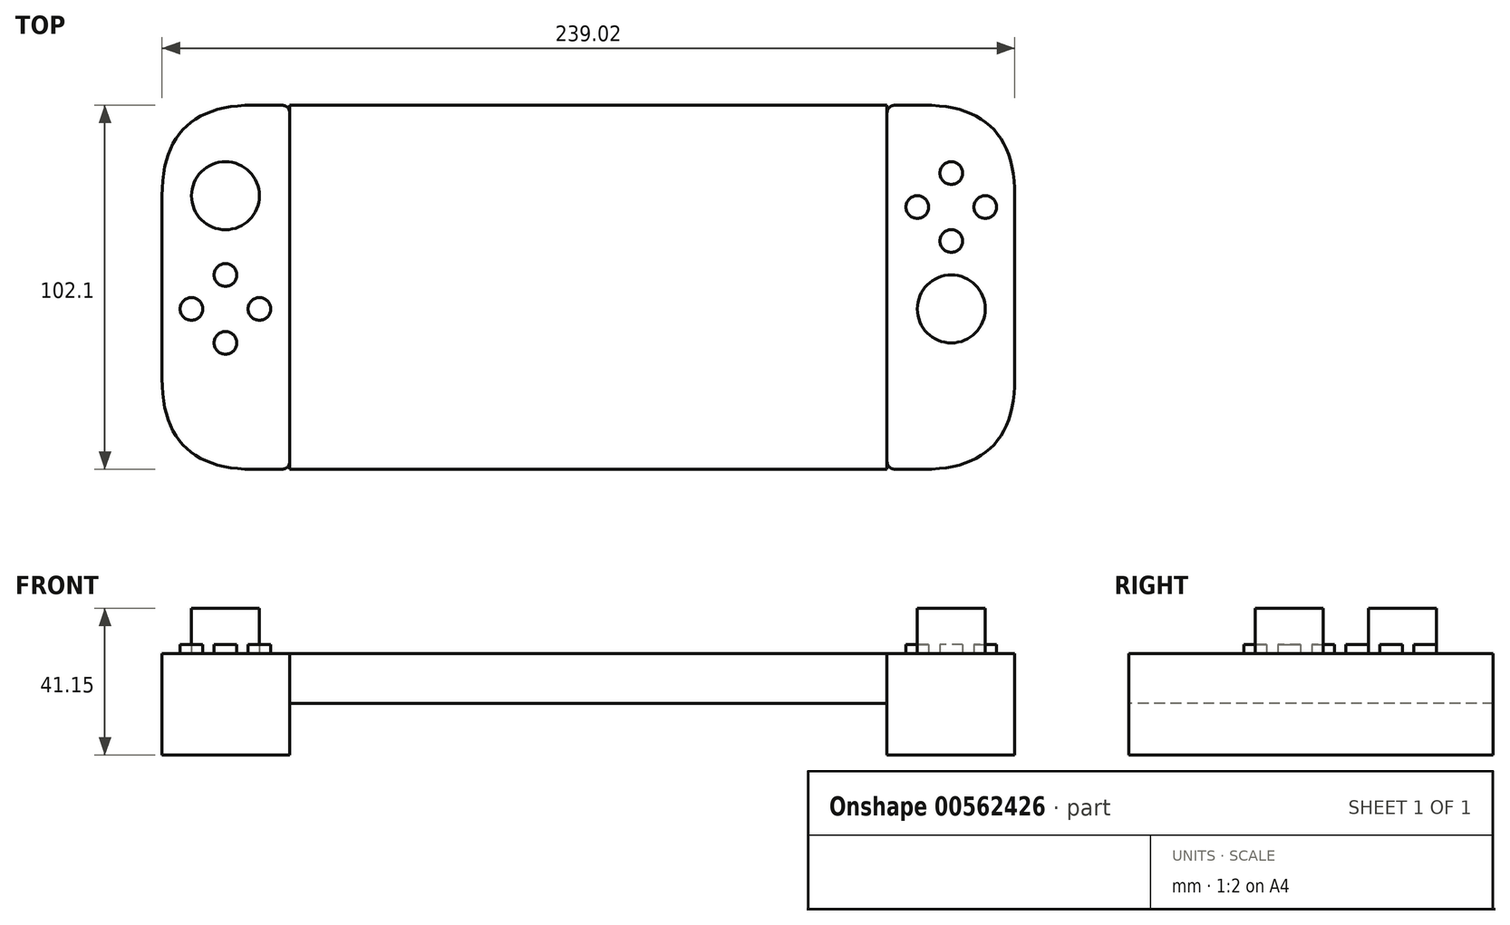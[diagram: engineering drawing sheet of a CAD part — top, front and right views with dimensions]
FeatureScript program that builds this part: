
annotation { "Feature Type Name" : "Feature", "Feature Type Description" : "" }
export const myFeature = defineFeature(function(context is Context, id is Id, definition is map)
    precondition{}
    {
        {
            var Q0;
            Q0=qCreatedBy(makeId("Top.planeOp"),FACE);
            var sketch = newSketch(context, id + "F0", { "sketchPlane" : qUnion([Q0])});
            skLineSegment(sketch, "E0.bottom", {"start": v(83.7, 51.05) * mm, "end": v(-83.7, 51.05) * mm});
            skLineSegment(sketch, "E0.top", {"start": v(83.7, -51.05) * mm, "end": v(-83.7, -51.05) * mm});
            skLineSegment(sketch, "E0.left", {"start": v(83.7, 51.05) * mm, "end": v(83.7, -51.05) * mm});
            skLineSegment(sketch, "E0.right", {"start": v(-83.7, 51.05) * mm, "end": v(-83.7, -51.05) * mm});
            skPoint(sketch, "E0.middle", {"position": v(0, 0) * mm});
            skSolve(sketch);
        }
        {
            var Q0;
            Q0=makeQuery(id+"F0.imprint","IMPRINT",FACE,{"disambiguationData":[TD([[makeQuery(id+"F0.imprint","IMPRINT",EDGE,{"derivedFrom":sQuery(id+"F0.wireOp",EDGE,"E0.bottom")}),1.0]])]});
            extrude(context, id + "F1", {"entities" : qUnion([Q0]), "depth" : 13.97 * mm, "offsetDistance" : 25.4 * mm});
        }
        {
            var Q0;
            Q0=makeQuery(id+"F1.opExtrude","CAP_FACE",FACE,{"disambiguationData":[OSD([sQuery(id+"F0.wireOp",EDGE,"E0.bottom"),sQuery(id+"F0.wireOp",EDGE,"E0.top"),sQuery(id+"F0.wireOp",EDGE,"E0.left"),sQuery(id+"F0.wireOp",EDGE,"E0.right")])],"isStart":false});
            var sketch = newSketch(context, id + "F2", { "sketchPlane" : qUnion([Q0])});
            skLineSegment(sketch, "E1.bottom", {"start": v(-83.7, 51.05) * mm, "end": v(-119.5, 51.05) * mm});
            skLineSegment(sketch, "E1.top", {"start": v(-83.7, -51.05) * mm, "end": v(-119.5, -51.05) * mm});
            skLineSegment(sketch, "E1.left", {"start": v(-83.7, 51.05) * mm, "end": v(-83.7, -51.05) * mm});
            skLineSegment(sketch, "E1.right", {"start": v(-119.5, 51.05) * mm, "end": v(-119.5, -51.05) * mm});
            skSolve(sketch);
        }
        {
            var Q0;
            Q0=makeQuery(id+"F2.imprint","IMPRINT",FACE,{"disambiguationData":[TD([[makeQuery(id+"F2.imprint","IMPRINT",EDGE,{"derivedFrom":sQuery(id+"F2.wireOp",EDGE,"E1.bottom")}),1.0]])]});
            extrude(context, id + "F3", {"entities" : qUnion([Q0]), "oppositeDirection" : true, "depth" : 28.45 * mm, "offsetDistance" : 25.4 * mm});
        }
        {
            var Q0;
            Q0=makeQuery(id+"F1.opExtrude","CAP_FACE",FACE,{"disambiguationData":[OSD([sQuery(id+"F0.wireOp",EDGE,"E0.bottom"),sQuery(id+"F0.wireOp",EDGE,"E0.top"),sQuery(id+"F0.wireOp",EDGE,"E0.left"),sQuery(id+"F0.wireOp",EDGE,"E0.right")])],"isStart":false});
            var sketch = newSketch(context, id + "F4", { "sketchPlane" : qUnion([Q0])});
            skLineSegment(sketch, "E2.bottom", {"start": v(83.7, 51.05) * mm, "end": v(119.5, 51.05) * mm});
            skLineSegment(sketch, "E2.top", {"start": v(83.7, -51.05) * mm, "end": v(119.5, -51.05) * mm});
            skLineSegment(sketch, "E2.left", {"start": v(83.7, 51.05) * mm, "end": v(83.7, -51.05) * mm});
            skLineSegment(sketch, "E2.right", {"start": v(119.5, 51.05) * mm, "end": v(119.5, -51.05) * mm});
            skSolve(sketch);
        }
        {
            var Q0;
            Q0=makeQuery(id+"F4.imprint","IMPRINT",FACE,{"disambiguationData":[TD([[makeQuery(id+"F4.imprint","IMPRINT",EDGE,{"derivedFrom":sQuery(id+"F4.wireOp",EDGE,"E2.bottom")}),-1.0]])]});
            extrude(context, id + "F5", {"entities" : qUnion([Q0]), "oppositeDirection" : true, "depth" : 28.45 * mm, "offsetDistance" : 25.4 * mm});
        }
        {
            var Q0;
            Q0=makeQuery(id+"F3.opExtrude","SWEPT_EDGE",EDGE,{"disambiguationData":[OSD([sQuery(id+"F2.wireOp",EDGE,"E1.bottom"),sQuery(id+"F2.wireOp",EDGE,"E1.right")])]});
            var Q1;
            Q1=makeQuery(id+"F3.opExtrude","SWEPT_EDGE",EDGE,{"disambiguationData":[OSD([sQuery(id+"F2.wireOp",EDGE,"E1.top"),sQuery(id+"F2.wireOp",EDGE,"E1.right")])]});
            var Q2;
            Q2=makeQuery(id+"F5.opExtrude","SWEPT_EDGE",EDGE,{"disambiguationData":[OSD([sQuery(id+"F4.wireOp",EDGE,"E2.bottom"),sQuery(id+"F4.wireOp",EDGE,"E2.right")])]});
            var Q3;
            Q3=makeQuery(id+"F5.opExtrude","SWEPT_EDGE",EDGE,{"disambiguationData":[OSD([sQuery(id+"F4.wireOp",EDGE,"E2.top"),sQuery(id+"F4.wireOp",EDGE,"E2.right")])]});
            fillet(context, id + "F6", {"entities" : qUnion([Q0, Q1, Q2, Q3]), "radius" : 25.4 * mm, "tangentPropagation" : true, "rho" : 0.5, "crossSection" : FilletCrossSection.CONIC, "allowEdgeOverflow" : false});
        }
        {
            var Q0;
            Q0=makeQuery(id+"F3.opExtrude","SWEPT_EDGE",EDGE,{"disambiguationData":[OSD([sQuery(id+"F0.wireOp",EDGE,"E0.bottom"),sQuery(id+"F2.wireOp",EDGE,"E1.bottom"),sQuery(id+"F2.wireOp",EDGE,"E1.left")])]});
            var Q1;
            Q1=makeQuery(id+"F5.opExtrude","SWEPT_EDGE",EDGE,{"disambiguationData":[OSD([sQuery(id+"F0.wireOp",EDGE,"E0.bottom"),sQuery(id+"F4.wireOp",EDGE,"E2.bottom"),sQuery(id+"F4.wireOp",EDGE,"E2.left")])]});
            var Q2;
            Q2=makeQuery(id+"F3.opExtrude","SWEPT_EDGE",EDGE,{"disambiguationData":[OSD([sQuery(id+"F0.wireOp",EDGE,"E0.top"),sQuery(id+"F2.wireOp",EDGE,"E1.top"),sQuery(id+"F2.wireOp",EDGE,"E1.left")])]});
            var Q3;
            Q3=makeQuery(id+"F5.opExtrude","SWEPT_EDGE",EDGE,{"disambiguationData":[OSD([sQuery(id+"F0.wireOp",EDGE,"E0.top"),sQuery(id+"F4.wireOp",EDGE,"E2.top"),sQuery(id+"F4.wireOp",EDGE,"E2.left")])]});
            fillet(context, id + "F7", {"entities" : qUnion([Q0, Q1, Q2, Q3]), "radius" : 2.54 * mm, "tangentPropagation" : true, "rho" : 0.5, "crossSection" : FilletCrossSection.CONIC, "allowEdgeOverflow" : false});
        }
        {
            var Q0;
            Q0=makeQuery(id+"F3.opExtrude","CAP_FACE",FACE,{"disambiguationData":[OSD([sQuery(id+"F2.wireOp",EDGE,"E1.bottom"),sQuery(id+"F2.wireOp",EDGE,"E1.top"),sQuery(id+"F2.wireOp",EDGE,"E1.left"),sQuery(id+"F2.wireOp",EDGE,"E1.right")])],"isStart":true});
            var sketch = newSketch(context, id + "F8", { "sketchPlane" : qUnion([Q0])});
            skCircle(sketch, "E3", {"center": v(-101.73, 25.65) * mm, "radius": 9.53 * mm});
            skSolve(sketch);
        }
        {
            var Q0;
            Q0=makeQuery(id+"F8.imprint","IMPRINT",FACE,{"disambiguationData":[TD([[makeQuery(id+"F8.imprint","IMPRINT",EDGE,{"derivedFrom":sQuery(id+"F8.wireOp",EDGE,"E3")}),1.0]])]});
            extrude(context, id + "F9", {"entities" : qUnion([Q0]), "depth" : 12.7 * mm, "offsetDistance" : 25.4 * mm});
        }
        {
            var Q0;
            Q0=makeQuery(id+"F3.opExtrude","CAP_FACE",FACE,{"disambiguationData":[OSD([sQuery(id+"F2.wireOp",EDGE,"E1.bottom"),sQuery(id+"F2.wireOp",EDGE,"E1.top"),sQuery(id+"F2.wireOp",EDGE,"E1.left"),sQuery(id+"F2.wireOp",EDGE,"E1.right")])],"isStart":true});
            var sketch = newSketch(context, id + "F10", { "sketchPlane" : qUnion([Q0])});
            skCircle(sketch, "E4", {"center": v(-101.73, 3.43) * mm, "radius": 3.18 * mm});
            skSolve(sketch);
        }
        {
            var Q0;
            Q0=makeQuery(id+"F10.imprint","IMPRINT",FACE,{"disambiguationData":[TD([[makeQuery(id+"F10.imprint","IMPRINT",EDGE,{"derivedFrom":sQuery(id+"F10.wireOp",EDGE,"E4")}),-1.0]])]});
            var sketch = newSketch(context, id + "F11", { "sketchPlane" : qUnion([Q0])});
            skCircle(sketch, "E5", {"center": v(-101.73, -15.62) * mm, "radius": 3.18 * mm});
            skSolve(sketch);
        }
        {
            var Q0;
            Q0=makeQuery(id+"F10.imprint","IMPRINT",FACE,{"disambiguationData":[TD([[makeQuery(id+"F10.imprint","IMPRINT",EDGE,{"derivedFrom":sQuery(id+"F10.wireOp",EDGE,"E4")}),-1.0]])]});
            var sketch = newSketch(context, id + "F12", { "sketchPlane" : qUnion([Q0])});
            skCircle(sketch, "E6", {"center": v(-92.2, -6.1) * mm, "radius": 3.18 * mm});
            skSolve(sketch);
        }
        {
            var Q0;
            Q0=makeQuery(id+"F10.imprint","IMPRINT",FACE,{"disambiguationData":[TD([[makeQuery(id+"F10.imprint","IMPRINT",EDGE,{"derivedFrom":sQuery(id+"F10.wireOp",EDGE,"E4")}),-1.0]])]});
            var sketch = newSketch(context, id + "F13", { "sketchPlane" : qUnion([Q0])});
            skCircle(sketch, "E7", {"center": v(-111.25, -6.1) * mm, "radius": 3.18 * mm});
            skSolve(sketch);
        }
        {
            var Q0;
            Q0=makeQuery(id+"F10.imprint","IMPRINT",FACE,{"disambiguationData":[TD([[makeQuery(id+"F10.imprint","IMPRINT",EDGE,{"derivedFrom":sQuery(id+"F10.wireOp",EDGE,"E4")}),1.0]])]});
            var Q1;
            Q1=sQuery(id+"F10.wireOp",EDGE,"E4");
            extrude(context, id + "F14", {"entities" : qUnion([Q0]), "surfaceEntities" : qUnion([Q1]), "depth" : 2.54 * mm, "offsetDistance" : 25.4 * mm});
        }
        {
            var Q0;
            Q0=makeQuery(id+"F11.imprint","IMPRINT",FACE,{"disambiguationData":[TD([[makeQuery(id+"F11.imprint","IMPRINT",EDGE,{"derivedFrom":sQuery(id+"F11.wireOp",EDGE,"E5")}),1.0]])]});
            var Q1;
            Q1=makeQuery(id+"F12.imprint","IMPRINT",FACE,{"disambiguationData":[TD([[makeQuery(id+"F12.imprint","IMPRINT",EDGE,{"derivedFrom":sQuery(id+"F12.wireOp",EDGE,"E6")}),1.0]])]});
            extrude(context, id + "F15", {"entities" : qUnion([Q0, Q1]), "depth" : 2.54 * mm, "offsetDistance" : 25.4 * mm});
        }
        {
            var Q0;
            Q0=makeQuery(id+"F13.imprint","IMPRINT",FACE,{"disambiguationData":[TD([[makeQuery(id+"F13.imprint","IMPRINT",EDGE,{"derivedFrom":sQuery(id+"F13.wireOp",EDGE,"E7")}),1.0]])]});
            var Q1;
            Q1=sQuery(id+"F13.wireOp",EDGE,"E7");
            extrude(context, id + "F16", {"entities" : qUnion([Q0]), "surfaceEntities" : qUnion([Q1]), "depth" : 2.54 * mm, "offsetDistance" : 25.4 * mm});
        }
        {
            var Q0;
            Q0=makeQuery(id+"F5.opExtrude","CAP_FACE",FACE,{"disambiguationData":[OSD([sQuery(id+"F4.wireOp",EDGE,"E2.bottom"),sQuery(id+"F4.wireOp",EDGE,"E2.top"),sQuery(id+"F4.wireOp",EDGE,"E2.left"),sQuery(id+"F4.wireOp",EDGE,"E2.right")])],"isStart":true});
            var sketch = newSketch(context, id + "F17", { "sketchPlane" : qUnion([Q0])});
            skCircle(sketch, "E8", {"center": v(101.73, 32) * mm, "radius": 3.18 * mm});
            skSolve(sketch);
        }
        {
            var Q0;
            Q0=makeQuery(id+"F17.imprint","IMPRINT",FACE,{"disambiguationData":[TD([[makeQuery(id+"F17.imprint","IMPRINT",EDGE,{"derivedFrom":sQuery(id+"F17.wireOp",EDGE,"E8")}),-1.0]])]});
            var sketch = newSketch(context, id + "F18", { "sketchPlane" : qUnion([Q0])});
            skCircle(sketch, "E9", {"center": v(111.25, 22.48) * mm, "radius": 3.18 * mm});
            skSolve(sketch);
        }
        {
            var Q0;
            Q0=makeQuery(id+"F17.imprint","IMPRINT",FACE,{"disambiguationData":[TD([[makeQuery(id+"F17.imprint","IMPRINT",EDGE,{"derivedFrom":sQuery(id+"F17.wireOp",EDGE,"E8")}),-1.0]])]});
            var sketch = newSketch(context, id + "F19", { "sketchPlane" : qUnion([Q0])});
            skCircle(sketch, "E10", {"center": v(92.2, 22.48) * mm, "radius": 3.18 * mm});
            skSolve(sketch);
        }
        {
            var Q0;
            Q0=makeQuery(id+"F17.imprint","IMPRINT",FACE,{"disambiguationData":[TD([[makeQuery(id+"F17.imprint","IMPRINT",EDGE,{"derivedFrom":sQuery(id+"F17.wireOp",EDGE,"E8")}),-1.0]])]});
            var sketch = newSketch(context, id + "F20", { "sketchPlane" : qUnion([Q0])});
            skCircle(sketch, "E11", {"center": v(101.73, 12.95) * mm, "radius": 3.18 * mm});
            skSolve(sketch);
        }
        {
            var Q0;
            Q0=makeQuery(id+"F17.imprint","IMPRINT",FACE,{"disambiguationData":[TD([[makeQuery(id+"F17.imprint","IMPRINT",EDGE,{"derivedFrom":sQuery(id+"F17.wireOp",EDGE,"E8")}),-1.0]])]});
            var sketch = newSketch(context, id + "F21", { "sketchPlane" : qUnion([Q0])});
            skCircle(sketch, "E12", {"center": v(101.73, -6.1) * mm, "radius": 9.53 * mm});
            skSolve(sketch);
        }
        {
            var Q0;
            Q0=makeQuery(id+"F17.imprint","IMPRINT",FACE,{"disambiguationData":[TD([[makeQuery(id+"F17.imprint","IMPRINT",EDGE,{"derivedFrom":sQuery(id+"F17.wireOp",EDGE,"E8")}),1.0]])]});
            extrude(context, id + "F22", {"entities" : qUnion([Q0]), "depth" : 2.54 * mm, "offsetDistance" : 25.4 * mm});
        }
        {
            var Q0;
            Q0=makeQuery(id+"F19.imprint","IMPRINT",FACE,{"disambiguationData":[TD([[makeQuery(id+"F19.imprint","IMPRINT",EDGE,{"derivedFrom":sQuery(id+"F19.wireOp",EDGE,"E10")}),1.0]])]});
            var Q1;
            Q1=sQuery(id+"F19.wireOp",EDGE,"E10");
            extrude(context, id + "F23", {"entities" : qUnion([Q0]), "surfaceEntities" : qUnion([Q1]), "depth" : 2.54 * mm, "offsetDistance" : 25.4 * mm});
        }
        {
            var Q0;
            Q0=makeQuery(id+"F20.imprint","IMPRINT",FACE,{"disambiguationData":[TD([[makeQuery(id+"F20.imprint","IMPRINT",EDGE,{"derivedFrom":sQuery(id+"F20.wireOp",EDGE,"E11")}),1.0]])]});
            extrude(context, id + "F24", {"entities" : qUnion([Q0]), "depth" : 2.54 * mm, "offsetDistance" : 25.4 * mm});
        }
        {
            var Q0;
            Q0=makeQuery(id+"F21.imprint","IMPRINT",FACE,{"disambiguationData":[TD([[makeQuery(id+"F21.imprint","IMPRINT",EDGE,{"derivedFrom":sQuery(id+"F21.wireOp",EDGE,"E12")}),1.0]])]});
            var Q1;
            Q1=sQuery(id+"F18.wireOp",EDGE,"E9");
            extrude(context, id + "F25", {"entities" : qUnion([Q0]), "surfaceEntities" : qUnion([Q1]), "depth" : 12.7 * mm, "offsetDistance" : 25.4 * mm});
        }
        {
            var Q0;
            Q0=makeQuery(id+"F5.opExtrude","CAP_FACE",FACE,{"disambiguationData":[OSD([sQuery(id+"F4.wireOp",EDGE,"E2.bottom"),sQuery(id+"F4.wireOp",EDGE,"E2.top"),sQuery(id+"F4.wireOp",EDGE,"E2.left"),sQuery(id+"F4.wireOp",EDGE,"E2.right")])],"isStart":true});
            var sketch = newSketch(context, id + "F26", { "sketchPlane" : qUnion([Q0])});
            skCircle(sketch, "E13", {"center": v(111.25, 22.48) * mm, "radius": 3.17 * mm});
            skSolve(sketch);
        }
        {
            var Q0;
            Q0=makeQuery(id+"F26.imprint","IMPRINT",FACE,{"disambiguationData":[TD([[makeQuery(id+"F26.imprint","IMPRINT",EDGE,{"derivedFrom":sQuery(id+"F26.wireOp",EDGE,"E13")}),1.0]])]});
            extrude(context, id + "F27", {"entities" : qUnion([Q0]), "depth" : 2.54 * mm, "offsetDistance" : 25.4 * mm});
        }
    });
